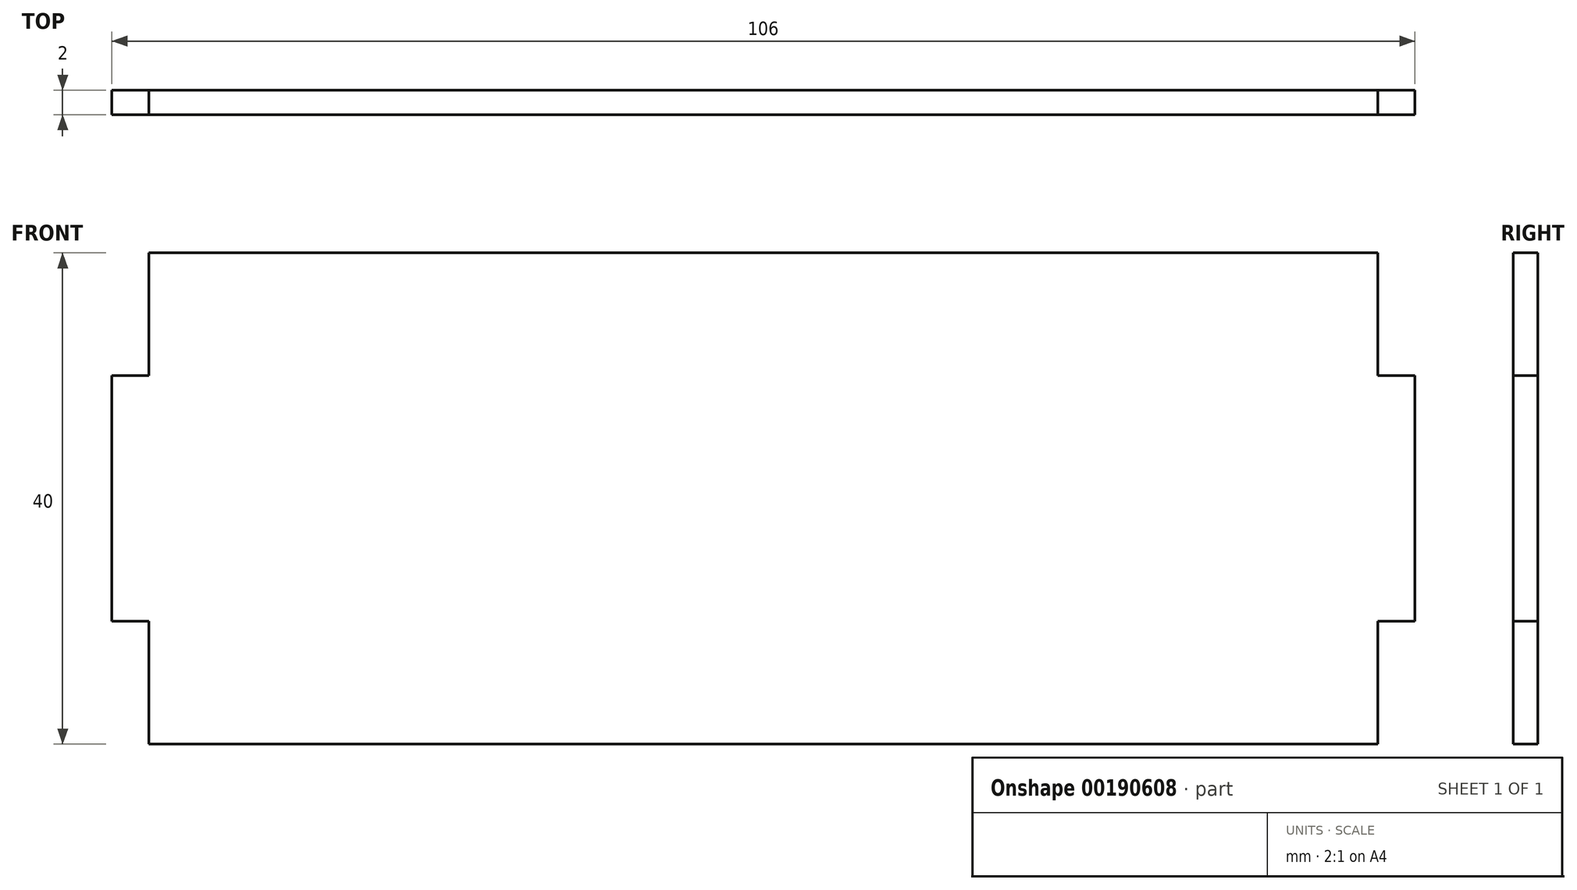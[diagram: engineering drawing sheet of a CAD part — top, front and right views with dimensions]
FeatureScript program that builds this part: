
annotation { "Feature Type Name" : "Feature", "Feature Type Description" : "" }
export const myFeature = defineFeature(function(context is Context, id is Id, definition is map)
    precondition{}
    {
        {
            var Q0;
            Q0=qCreatedBy(makeId("Front.planeOp"),FACE);
            var sketch = newSketch(context, id + "F0", { "sketchPlane" : qUnion([Q0])});
            skLineSegment(sketch, "E0.bottom", {"start": v(50, -20) * mm, "end": v(-50, -20) * mm});
            skLineSegment(sketch, "E0.top", {"start": v(50, 20) * mm, "end": v(-50, 20) * mm});
            skLineSegment(sketch, "E0.left", {"start": v(50, -20) * mm, "end": v(50, -10) * mm});
            skPoint(sketch, "E0.middle", {"position": v(0, 0) * mm});
            skLineSegment(sketch, "E1.bottom", {"start": v(50, -10) * mm, "end": v(53, -10) * mm});
            skLineSegment(sketch, "E1.top", {"start": v(50, 10) * mm, "end": v(53, 10) * mm});
            skLineSegment(sketch, "E1.right", {"start": v(53, -10) * mm, "end": v(53, 10) * mm});
            skLineSegment(sketch, "E2", {"start": v(0, 20) * mm, "end": v(0, -20) * mm, "construction": true});
            skLineSegment(sketch, "E3.trimOffspring", {"start": v(50, 10) * mm, "end": v(50, 20) * mm});
            skLineSegment(sketch, "E4.MirrorCS", {"start": v(-50, 20) * mm, "end": v(50, 20) * mm});
            skLineSegment(sketch, "E5.MirrorCS", {"start": v(-50, 10) * mm, "end": v(-50, 20) * mm});
            skLineSegment(sketch, "E6.MirrorCS", {"start": v(-50, 10) * mm, "end": v(-53, 10) * mm});
            skLineSegment(sketch, "E7.MirrorCS", {"start": v(-50, -10) * mm, "end": v(-53, -10) * mm});
            skLineSegment(sketch, "E8.MirrorCS", {"start": v(-50, -20) * mm, "end": v(-50, -10) * mm});
            skLineSegment(sketch, "E9.MirrorCS", {"start": v(-53, -10) * mm, "end": v(-53, 10) * mm});
            skSolve(sketch);
        }
        {
            var Q0;
            Q0=makeQuery(id+"F0.imprint","IMPRINT",FACE,{"disambiguationData":[TD([[makeQuery(id+"F0.imprint","IMPRINT",EDGE,{"derivedFrom":sQuery(id+"F0.wireOp",EDGE,"E0.bottom")}),-1.0]])]});
            extrude(context, id + "F1", {"entities" : qUnion([Q0]), "depth" : 2 * mm});
        }
    });
